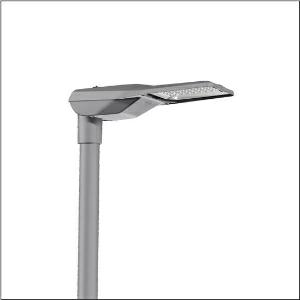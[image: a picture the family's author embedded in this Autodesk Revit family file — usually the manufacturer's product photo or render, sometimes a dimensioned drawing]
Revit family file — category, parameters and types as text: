
# Revit family: streetlight_sl_21_iq_mini___st1_0a_5xe2d31v08hb_a16f
name_source: partatom
category: Lighting Fixtures
units: mm (PartAtom-declared; Revit-internal decimal feet)

## family parameters
Cut with Voids When Loaded = No
Host = Face
Light Source = No
Part Type = Normal
Room Calculation Point = No
Round Connector Dimension = Use Diameter
Shared = No

## types (1)
- --- (1 x LED, 9750 lm, 71 W, 3000K)
    Apparent Load = 71 VA
    CIE Flux Codes = 37 72 97 100 100
    Color Rendering = 70
    Color Temperature = 3000K
    Default Elevation = 1800 mm
    Description = Streetlight SL 21 iQ mini, mast luminaire, primary light control with lens, of PMMA, primary optical cover: cover, of toughened safety glass, transparent, light distribution: ST1.0a, light emission: direct distribution, primary light characteristic: asymmetric, installation type: post-top, side-entry, LED, High Power LED, rated luminous flux: 9.750lm, luminous efficacy: 137lm/W, light colour: 730, colour temperature: 3000K, control: presetting dimming logarithmic, Street-Remote, Auto-Match, Temp-Guard, Lumen-Switch, Night-Set, Smart-Wire, Light-Fading, Desk-Remote (wireless, voltage-free reading and setting of iQ features in the workshop via application-optimized NFC function/RFID function), optimised constant luminous flux control (CLO 2.0), mains connection: 220..240V, AC, 50/60Hz, start of lifetime: 71W, end of service life: 75W, reduction: 30W, luminaire housing, of diecast aluminium, powder-coated, Siteco® metallic grey (DB 702S), corrosivity category C5 mid according to DIN EN ISO 12944, please order mast flange separately, inclination adjustable: 0°, 5°, 10°, 15°, sealing non-destructively replaceable, multi-level sealing system, length: 628mm, width: 235mm, height: 110mm, mast flange for spigot size: 42mm (side-entry): 5XC10008XM4, 60/48mm (side-entry/post-top): 5XC10108XM2, 76/60mm (side-entry/post-top): 5XC10108XM1, Smart Interface above, protection rating (complete): IP66, insulation class (complete): insulation class II (safety insulation), certification: CE, ENEC, ENEC+, VDE, impact resistance: IK09, permissible operating ambient temperature for outdoor applications: -40..+50°C, standard-compliant lighting for roads and squares, packaging unit: 1 piece

Light Distribution: ST1.0a
    Height = 110 mm
    Lamp = 1 x LED
    Lamp Light Flux = 9750 lm
    Lamp Power = 71 W
    Lamp count = 1
    Length = 625 mm
    Luminous efficacy = 137 lm/W
    Manufacturer = Siteco
    ModVariant = No
    Model = 5XE2D31V08HB
    Number of Poles = 1
    OnlyDefault = Yes
    Power Factor = 1
    Product Name = Streetlight SL 21 iQ mini | ST1.0a
    Product group = mast luminaire | pylon top
    ProductGroupID = 6100
    Protection Class = Protection class II
    Protection Degree = IP 66
    RLX_Detail_Level = 1
    RLX_Emergency_Light_Flux = 0 lm
    RLX_Emergency_Type = 0
    RLX_Emergency_Type_DB = No
    RlxData = <blob elided: 92565 chars, md5=11925900>
    Socket = socket
    Standby Power = 0 W
    System Light Flux = 9750 lm
    System Power = 71 W
    Type Comments = factory setting: luminous flux: 100 % | dim-lin: 254 | 716 mA
    Type Image = l_1003515.jpg
    URL = http://relux.com
    VarID = @adj_045149
    Voltage = 0 V
    Weight = 0.00 kg
    Width = 234 mm

## geometry (parser evidence)
native form markers: Blend x4, Sweep x10
no freeform markers — native parametric forms only
